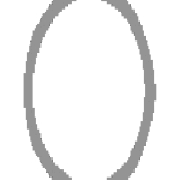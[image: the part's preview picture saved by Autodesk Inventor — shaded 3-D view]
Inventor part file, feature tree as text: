
AUTODESK INVENTOR PART (.ipt)
format: ipt  version: 2021 (Build 250183000, 183)  size: 109,568 bytes
history: native  units: in
note: dims shown in document units (in); Inventor stores cm internally (conversion verified against a paired STEP export)
features: other x4, sketch x3, plane x1
ambient origin geometry x8: Origin, YZ Plane, XZ Plane, XY Plane, X Axis, Y Axis, Z Axis, Center Point
bodies: Solid1 (feature_tree), Body (feature_tree)
feature tree (8):
  other  "Driven Length"
  other  "Frame Generator"
  other  "Start Plane"
  other  "End Plane"
  sketch  "Sketch"  dims[d2=21.1542in d4=-0.0in d5=21.1542in d6=0.12in d7=0.0in d10=90.0deg d9=21.1542in]
  sketch  "Sketch4"  dims[d0=1.0in]
  plane  "Work Plane4"
  sketch  "Sketch5"  dims[d1=0.065in]
